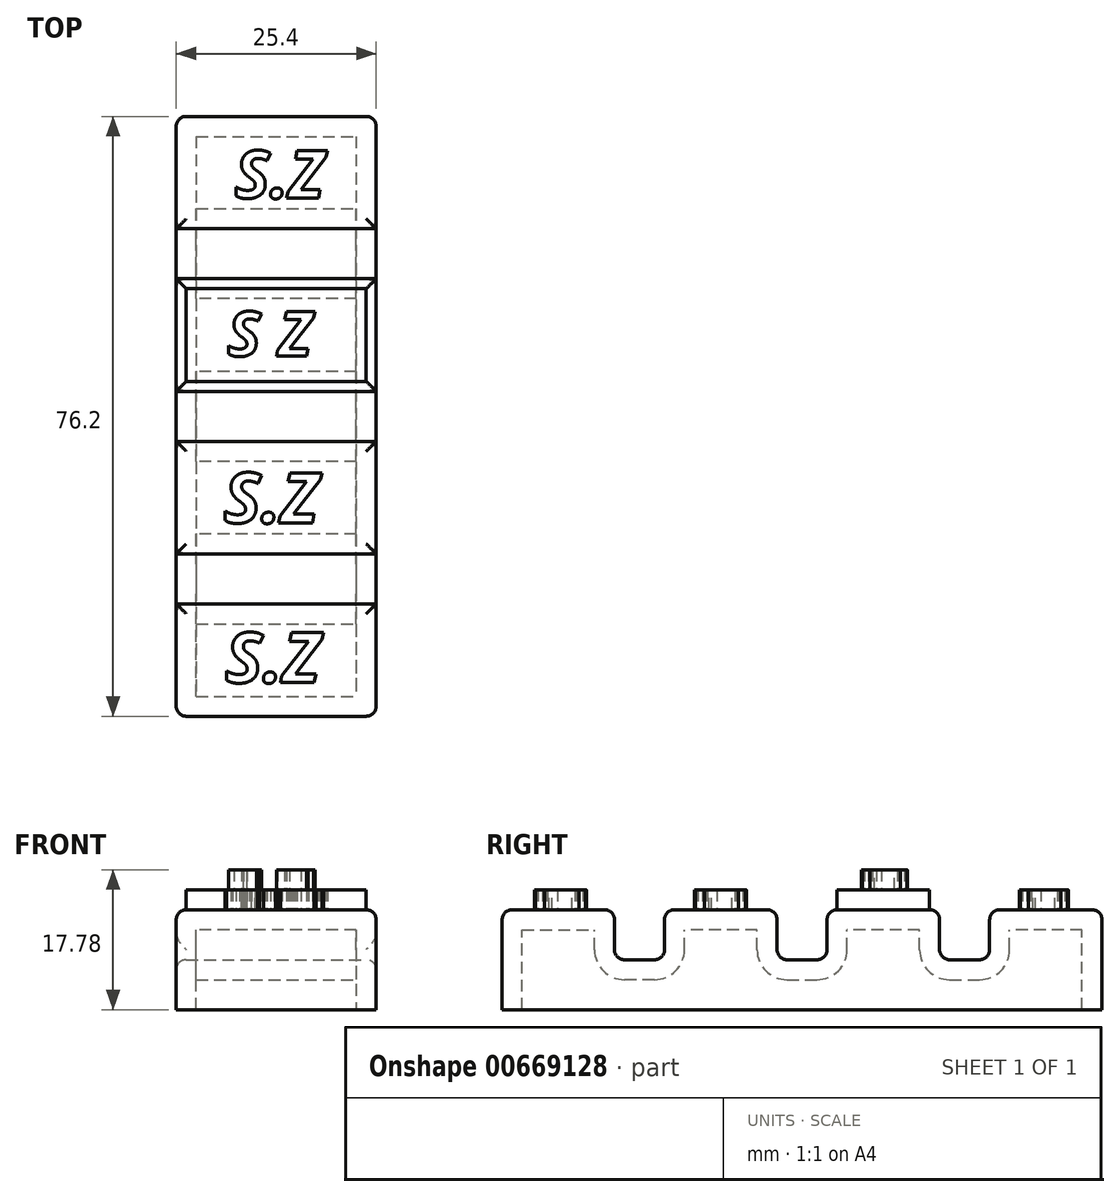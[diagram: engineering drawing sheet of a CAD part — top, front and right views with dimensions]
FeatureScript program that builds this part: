
annotation { "Feature Type Name" : "Feature", "Feature Type Description" : "" }
export const myFeature = defineFeature(function(context is Context, id is Id, definition is map)
    precondition{}
    {
        {
            var Q0;
            Q0=qCreatedBy(makeId("Top.planeOp"),FACE);
            var sketch = newSketch(context, id + "F0", { "sketchPlane" : qUnion([Q0])});
            skLineSegment(sketch, "E0.bottom", {"start": v(-12.7, 38.1) * mm, "end": v(12.7, 38.1) * mm});
            skLineSegment(sketch, "E0.top", {"start": v(-12.7, -38.1) * mm, "end": v(12.7, -38.1) * mm});
            skLineSegment(sketch, "E0.left", {"start": v(-12.7, 38.1) * mm, "end": v(-12.7, -38.1) * mm});
            skLineSegment(sketch, "E0.right", {"start": v(12.7, 38.1) * mm, "end": v(12.7, -38.1) * mm});
            skPoint(sketch, "E0.middle", {"position": v(0, 0) * mm});
            skSolve(sketch);
        }
        {
            var Q0;
            Q0 = qSketchRegion(id + "F0", true);
            extrude(context, id + "F1", {"entities" : qUnion([Q0]), "depth" : 12.7 * mm, "offsetDistance" : 25.4 * mm});
        }
        {
            var Q0;
            Q0=makeQuery(id+"F1.opExtrude","SWEPT_FACE",FACE,{"disambiguationData":[OSD([sQuery(id+"F0.wireOp",EDGE,"E0.right")])]});
            var sketch = newSketch(context, id + "F2", { "sketchPlane" : qUnion([Q0])});
            skLineSegment(sketch, "E1", {"start": v(-38.1, 6.35) * mm, "end": v(38.1, 6.35) * mm, "construction": true});
            skLineSegment(sketch, "E2.bottom", {"start": v(3.17, 6.35) * mm, "end": v(-3.18, 6.35) * mm});
            skLineSegment(sketch, "E2.top", {"start": v(3.17, 19.05) * mm, "end": v(-3.18, 19.05) * mm});
            skLineSegment(sketch, "E2.left", {"start": v(3.17, 6.35) * mm, "end": v(3.17, 19.05) * mm});
            skLineSegment(sketch, "E2.right", {"start": v(-3.18, 6.35) * mm, "end": v(-3.18, 19.05) * mm});
            skPoint(sketch, "E2.middle", {"position": v(0, 12.7) * mm});
            skLineSegment(sketch, "E3.bottom", {"start": v(-17.48, 6.35) * mm, "end": v(-23.83, 6.35) * mm});
            skLineSegment(sketch, "E3.top", {"start": v(-17.48, 19.05) * mm, "end": v(-23.83, 19.05) * mm});
            skLineSegment(sketch, "E3.left", {"start": v(-17.48, 6.35) * mm, "end": v(-17.48, 19.05) * mm});
            skLineSegment(sketch, "E3.right", {"start": v(-23.83, 6.35) * mm, "end": v(-23.83, 19.05) * mm});
            skPoint(sketch, "E3.middle", {"position": v(-20.65, 12.7) * mm});
            skLineSegment(sketch, "E4.bottom", {"start": v(23.83, 6.35) * mm, "end": v(17.48, 6.35) * mm});
            skLineSegment(sketch, "E4.top", {"start": v(23.83, 19.05) * mm, "end": v(17.48, 19.05) * mm});
            skLineSegment(sketch, "E4.left", {"start": v(23.83, 6.35) * mm, "end": v(23.83, 19.05) * mm});
            skLineSegment(sketch, "E4.right", {"start": v(17.48, 6.35) * mm, "end": v(17.48, 19.05) * mm});
            skPoint(sketch, "E4.middle", {"position": v(20.65, 12.7) * mm});
            skSolve(sketch);
        }
        {
            var Q0;
            Q0 = qSketchRegion(id + "F2", true);
            extrude(context, id + "F3", {"entities" : qUnion([Q0]), "operationType" : NewBodyOperationType.REMOVE, "endBound" : BoundingType.THROUGH_ALL, "oppositeDirection" : true, "depth" : 25.4 * mm, "offsetDistance" : 25.4 * mm});
        }
        {
            var Q0;
            {var subQ0=sQuery(id+"F0.wireOp",EDGE,"E0.top");var subQ1=sQuery(id+"F0.wireOp",EDGE,"E0.left");var subQ2=sQuery(id+"F0.wireOp",EDGE,"E0.right");Q0=makeQuery(id+"F3.boolean.opBoolean","SPLIT",FACE,{"disambiguationData":[TD([makeQuery(id+"F1.opExtrude","SWEPT_FACE",FACE,{"disambiguationData":[OSD([subQ0])]})])],"derivedFrom":makeQuery(id+"F1.opExtrude","CAP_FACE",FACE,{"disambiguationData":[OSD([sQuery(id+"F0.wireOp",EDGE,"E0.bottom"),subQ0,subQ1,subQ2])],"isStart":false})});}
            var Q1;
            {var subQ0=sQuery(id+"F0.wireOp",EDGE,"E0.left");var subQ1=sQuery(id+"F0.wireOp",EDGE,"E0.right");Q1=makeQuery(id+"F3.boolean.opBoolean","SPLIT",FACE,{"disambiguationData":[TD([makeQuery(id+"F3.opExtrude","SWEPT_FACE",FACE,{"disambiguationData":[OSD([sQuery(id+"F2.wireOp",EDGE,"E2.right")])]})])],"derivedFrom":makeQuery(id+"F1.opExtrude","CAP_FACE",FACE,{"disambiguationData":[OSD([sQuery(id+"F0.wireOp",EDGE,"E0.bottom"),sQuery(id+"F0.wireOp",EDGE,"E0.top"),subQ0,subQ1])],"isStart":false})});}
            var Q2;
            {var subQ0=sQuery(id+"F0.wireOp",EDGE,"E0.left");var subQ1=sQuery(id+"F0.wireOp",EDGE,"E0.right");Q2=makeQuery(id+"F3.boolean.opBoolean","SPLIT",FACE,{"disambiguationData":[TD([makeQuery(id+"F3.opExtrude","SWEPT_FACE",FACE,{"disambiguationData":[OSD([sQuery(id+"F2.wireOp",EDGE,"E2.left")])]})])],"derivedFrom":makeQuery(id+"F1.opExtrude","CAP_FACE",FACE,{"disambiguationData":[OSD([sQuery(id+"F0.wireOp",EDGE,"E0.bottom"),sQuery(id+"F0.wireOp",EDGE,"E0.top"),subQ0,subQ1])],"isStart":false})});}
            var Q3;
            {var subQ0=sQuery(id+"F0.wireOp",EDGE,"E0.bottom");var subQ1=sQuery(id+"F0.wireOp",EDGE,"E0.right");var subQ2=sQuery(id+"F0.wireOp",EDGE,"E0.left");Q3=makeQuery(id+"F3.boolean.opBoolean","SPLIT",FACE,{"disambiguationData":[TD([makeQuery(id+"F1.opExtrude","SWEPT_FACE",FACE,{"disambiguationData":[OSD([subQ0])]})])],"derivedFrom":makeQuery(id+"F1.opExtrude","CAP_FACE",FACE,{"disambiguationData":[OSD([subQ0,sQuery(id+"F0.wireOp",EDGE,"E0.top"),subQ2,subQ1])],"isStart":false})});}
            var Q4;
            Q4=makeQuery(id+"F3.boolean.opBoolean","COPY",EDGE,{"derivedFrom":makeQuery(id+"F3.opExtrude","SWEPT_EDGE",EDGE,{"disambiguationData":[OSD([sQuery(id+"F2.wireOp",EDGE,"E3.bottom"),sQuery(id+"F2.wireOp",EDGE,"E3.right")])]})});
            var Q5;
            Q5=makeQuery(id+"F3.boolean.opBoolean","COPY",FACE,{"derivedFrom":makeQuery(id+"F3.opExtrude","SWEPT_FACE",FACE,{"disambiguationData":[OSD([sQuery(id+"F2.wireOp",EDGE,"E2.bottom")])]})});
            var Q6;
            Q6=makeQuery(id+"F3.boolean.opBoolean","COPY",FACE,{"derivedFrom":makeQuery(id+"F3.opExtrude","SWEPT_FACE",FACE,{"disambiguationData":[OSD([sQuery(id+"F2.wireOp",EDGE,"E4.bottom")])]})});
            var Q7;
            Q7=makeQuery(id+"F3.boolean.opBoolean","COPY",FACE,{"derivedFrom":makeQuery(id+"F3.opExtrude","SWEPT_FACE",FACE,{"disambiguationData":[OSD([sQuery(id+"F2.wireOp",EDGE,"E3.bottom")])]})});
            var Q8;
            Q8=makeQuery(id+"F1.opExtrude","SWEPT_EDGE",EDGE,{"disambiguationData":[OSD([sQuery(id+"F0.wireOp",EDGE,"E0.bottom"),sQuery(id+"F0.wireOp",EDGE,"E0.right")])]});
            var Q9;
            Q9=makeQuery(id+"F1.opExtrude","SWEPT_EDGE",EDGE,{"disambiguationData":[OSD([sQuery(id+"F0.wireOp",EDGE,"E0.top"),sQuery(id+"F0.wireOp",EDGE,"E0.right")])]});
            var Q10;
            Q10=makeQuery(id+"F1.opExtrude","SWEPT_EDGE",EDGE,{"disambiguationData":[OSD([sQuery(id+"F0.wireOp",EDGE,"E0.top"),sQuery(id+"F0.wireOp",EDGE,"E0.left")])]});
            var Q11;
            Q11=makeQuery(id+"F1.opExtrude","SWEPT_EDGE",EDGE,{"disambiguationData":[OSD([sQuery(id+"F0.wireOp",EDGE,"E0.bottom"),sQuery(id+"F0.wireOp",EDGE,"E0.left")])]});
            fillet(context, id + "F4", {"entities" : qUnion([Q0, Q1, Q2, Q3, Q4, Q5, Q6, Q7, Q8, Q9, Q10, Q11]), "radius" : 1.27 * mm, "tangentPropagation" : true, "allowEdgeOverflow" : false});
        }
        {
            var Q0;
            Q0=makeQuery(id+"F1.opExtrude","CAP_FACE",FACE,{"disambiguationData":[OSD([sQuery(id+"F0.wireOp",EDGE,"E0.bottom"),sQuery(id+"F0.wireOp",EDGE,"E0.top"),sQuery(id+"F0.wireOp",EDGE,"E0.left"),sQuery(id+"F0.wireOp",EDGE,"E0.right")])],"isStart":true});
            shell(context, id + "F5", {"entities" : qUnion([Q0]), "thickness" : 2.54 * mm});
        }
        {
            var Q0;
            {var subQ0=sQuery(id+"F0.wireOp",EDGE,"E0.left");var subQ1=sQuery(id+"F0.wireOp",EDGE,"E0.right");Q0=makeQuery(id+"F3.boolean.opBoolean","SPLIT",FACE,{"disambiguationData":[TD([makeQuery(id+"F3.opExtrude","SWEPT_FACE",FACE,{"disambiguationData":[OSD([sQuery(id+"F2.wireOp",EDGE,"E2.left")])]})])],"derivedFrom":makeQuery(id+"F1.opExtrude","CAP_FACE",FACE,{"disambiguationData":[OSD([sQuery(id+"F0.wireOp",EDGE,"E0.bottom"),sQuery(id+"F0.wireOp",EDGE,"E0.top"),subQ0,subQ1])],"isStart":false})});}
            var sketch = newSketch(context, id + "F6", { "sketchPlane" : qUnion([Q0])});
            skText(sketch, "E5", { "text": "S.Z", "fontName": "OpenSans-BoldItalic.ttf"});
            skText(sketch, "E6", { "text": "S.Z", "fontName": "OpenSans-BoldItalic.ttf"});
            skText(sketch, "E7", { "text": "S.Z", "fontName": "OpenSans-BoldItalic.ttf"});
            const initialGuessF6  = {"E5": [-0.00618, 0.00764, 1, 0, 0.0057], "E6": [-0.00666, -0.01354, 1, 0, 0.00641], "E7": [-0.00645, -0.03384, 1, 0, 0.00641]};
            skSetInitialGuess(sketch, initialGuessF6);
            skSolve(sketch);
        }
        {
            var Q0;
            Q0 = qSketchRegion(id + "F6", true);
            extrude(context, id + "F7", {"entities" : qUnion([Q0]), "operationType" : NewBodyOperationType.ADD, "depth" : 2.54 * mm, "offsetDistance" : 25.4 * mm});
        }
        {
            var Q0;
            {var subQ0=sQuery(id+"F0.wireOp",EDGE,"E0.bottom");var subQ1=sQuery(id+"F0.wireOp",EDGE,"E0.right");var subQ2=sQuery(id+"F0.wireOp",EDGE,"E0.left");Q0=makeQuery(id+"F3.boolean.opBoolean","SPLIT",FACE,{"disambiguationData":[TD([makeQuery(id+"F1.opExtrude","SWEPT_FACE",FACE,{"disambiguationData":[OSD([subQ0])]})])],"derivedFrom":makeQuery(id+"F1.opExtrude","CAP_FACE",FACE,{"disambiguationData":[OSD([subQ0,sQuery(id+"F0.wireOp",EDGE,"E0.top"),subQ2,subQ1])],"isStart":false})});}
            var sketch = newSketch(context, id + "F8", { "sketchPlane" : qUnion([Q0])});
            skText(sketch, "E8", { "text": "S.Z", "fontName": "OpenSans-BoldItalic.ttf"});
            const initialGuessF8  = {"E8": [-0.00528, 0.02772, 1, 0, 0.00607]};
            skSetInitialGuess(sketch, initialGuessF8);
            skSolve(sketch);
        }
        {
            var Q0;
            Q0 = qSketchRegion(id + "F8", true);
            var Q1;
            {var subQ0=sQuery(id+"F0.wireOp",EDGE,"E0.left");var subQ1=sQuery(id+"F0.wireOp",EDGE,"E0.right");Q1=makeQuery(id+"F3.boolean.opBoolean","SPLIT",FACE,{"disambiguationData":[TD([makeQuery(id+"F3.opExtrude","SWEPT_FACE",FACE,{"disambiguationData":[OSD([sQuery(id+"F2.wireOp",EDGE,"E2.left")])]})])],"derivedFrom":makeQuery(id+"F1.opExtrude","CAP_FACE",FACE,{"disambiguationData":[OSD([sQuery(id+"F0.wireOp",EDGE,"E0.bottom"),sQuery(id+"F0.wireOp",EDGE,"E0.top"),subQ0,subQ1])],"isStart":false})});}
            var Q2;
            Q2=makeQuery(id+"F7.opExtrude","CAP_FACE",FACE,{"disambiguationData":[OSD([sQuery(id+"F6.wireOp",EDGE,"E5.sketch_text.stroke-0"),sQuery(id+"F6.wireOp",EDGE,"E5.sketch_text.stroke-1"),sQuery(id+"F6.wireOp",EDGE,"E5.sketch_text.stroke-2"),sQuery(id+"F6.wireOp",EDGE,"E5.sketch_text.stroke-3"),sQuery(id+"F6.wireOp",EDGE,"E5.sketch_text.stroke-4"),sQuery(id+"F6.wireOp",EDGE,"E5.sketch_text.stroke-5"),sQuery(id+"F6.wireOp",EDGE,"E5.sketch_text.stroke-6"),sQuery(id+"F6.wireOp",EDGE,"E5.sketch_text.stroke-7"),sQuery(id+"F6.wireOp",EDGE,"E5.sketch_text.stroke-8"),sQuery(id+"F6.wireOp",EDGE,"E5.sketch_text.stroke-9"),sQuery(id+"F6.wireOp",EDGE,"E5.sketch_text.stroke-10"),sQuery(id+"F6.wireOp",EDGE,"E5.sketch_text.stroke-11"),sQuery(id+"F6.wireOp",EDGE,"E5.sketch_text.stroke-12"),sQuery(id+"F6.wireOp",EDGE,"E5.sketch_text.stroke-13"),sQuery(id+"F6.wireOp",EDGE,"E5.sketch_text.stroke-14"),sQuery(id+"F6.wireOp",EDGE,"E5.sketch_text.stroke-15"),sQuery(id+"F6.wireOp",EDGE,"E5.sketch_text.stroke-16"),sQuery(id+"F6.wireOp",EDGE,"E5.sketch_text.stroke-17"),sQuery(id+"F6.wireOp",EDGE,"E5.sketch_text.stroke-18"),sQuery(id+"F6.wireOp",EDGE,"E5.sketch_text.stroke-19"),sQuery(id+"F6.wireOp",EDGE,"E5.sketch_text.stroke-20"),sQuery(id+"F6.wireOp",EDGE,"E5.sketch_text.stroke-21"),sQuery(id+"F6.wireOp",EDGE,"E5.sketch_text.stroke-22"),sQuery(id+"F6.wireOp",EDGE,"E5.sketch_text.stroke-23")])],"isStart":false});
            var Q3;
            Q3=makeQuery(id+"F7.opExtrude","CAP_FACE",FACE,{"disambiguationData":[OSD([sQuery(id+"F6.wireOp",EDGE,"E5.sketch_text.stroke-32"),sQuery(id+"F6.wireOp",EDGE,"E5.sketch_text.stroke-33"),sQuery(id+"F6.wireOp",EDGE,"E5.sketch_text.stroke-34"),sQuery(id+"F6.wireOp",EDGE,"E5.sketch_text.stroke-35"),sQuery(id+"F6.wireOp",EDGE,"E5.sketch_text.stroke-36"),sQuery(id+"F6.wireOp",EDGE,"E5.sketch_text.stroke-37"),sQuery(id+"F6.wireOp",EDGE,"E5.sketch_text.stroke-38"),sQuery(id+"F6.wireOp",EDGE,"E5.sketch_text.stroke-39"),sQuery(id+"F6.wireOp",EDGE,"E5.sketch_text.stroke-40"),sQuery(id+"F6.wireOp",EDGE,"E5.sketch_text.stroke-41")])],"isStart":false});
            extrude(context, id + "F9", {"entities" : qUnion([Q0, Q1, Q2, Q3]), "operationType" : NewBodyOperationType.ADD, "depth" : 2.54 * mm, "offsetDistance" : 25.4 * mm});
        }
    });
